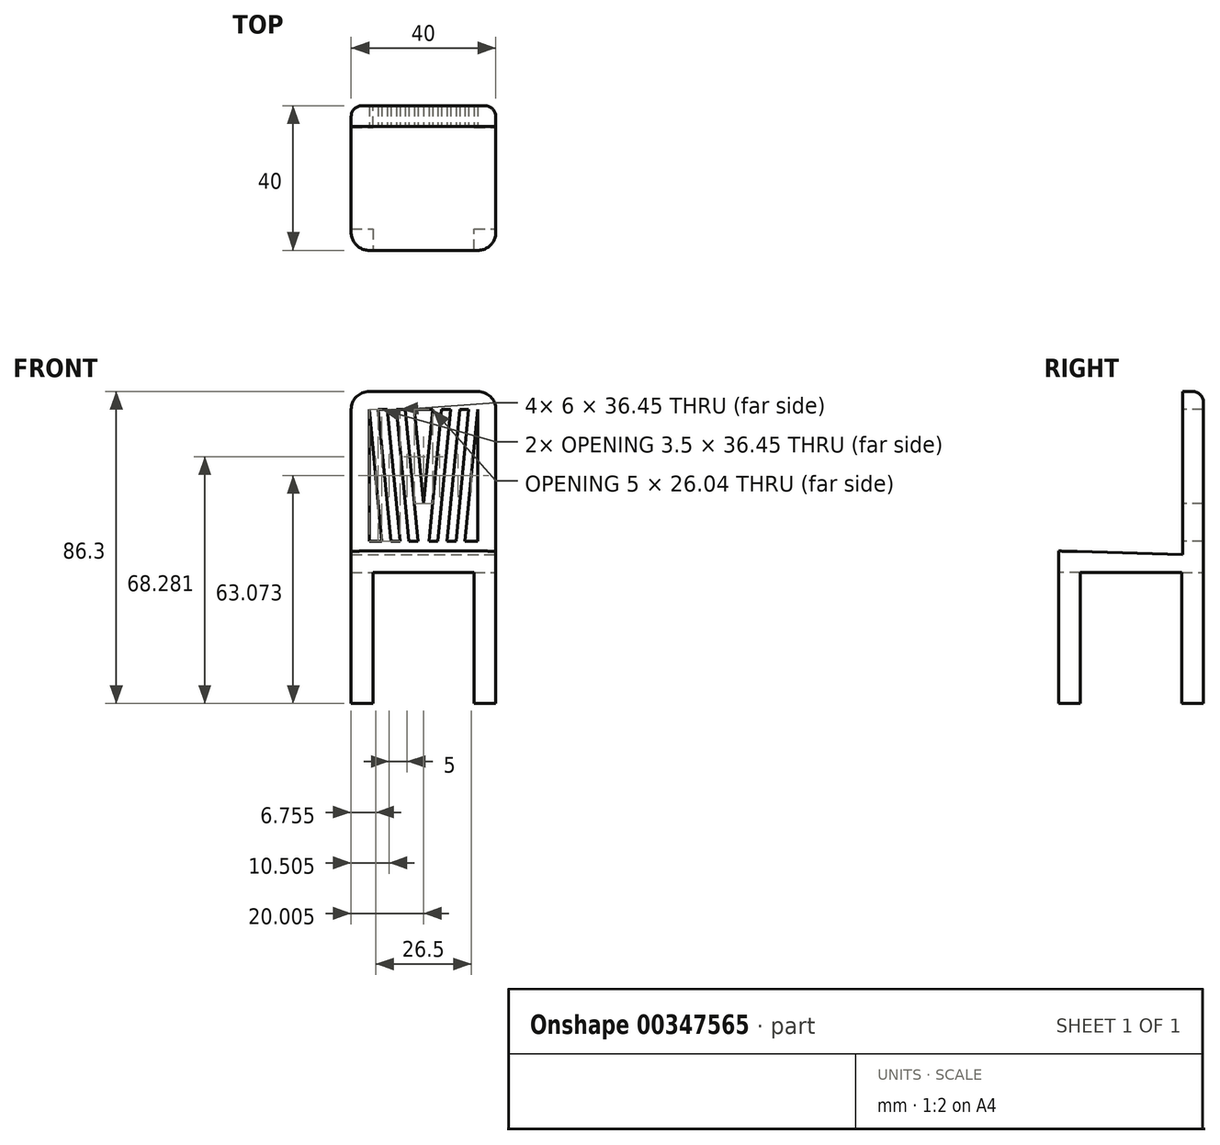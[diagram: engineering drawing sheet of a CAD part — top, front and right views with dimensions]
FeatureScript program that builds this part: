
annotation { "Feature Type Name" : "Feature", "Feature Type Description" : "" }
export const myFeature = defineFeature(function(context is Context, id is Id, definition is map)
    precondition{}
    {
        {
            var Q0;
            Q0=qCreatedBy(makeId("Top.planeOp"),FACE);
            var sketch = newSketch(context, id + "F0", { "sketchPlane" : qUnion([Q0])});
            skLineSegment(sketch, "E0", {"start": v(-30.46, 0) * mm, "end": v(-30.46, 30) * mm});
            skLineSegment(sketch, "E1", {"start": v(-30.46, 30) * mm, "end": v(9.54, 30) * mm});
            skLineSegment(sketch, "E2", {"start": v(9.54, 30) * mm, "end": v(9.54, -10) * mm});
            skLineSegment(sketch, "E3", {"start": v(9.54, -10) * mm, "end": v(-30.46, -10) * mm});
            skLineSegment(sketch, "E4", {"start": v(-30.46, -10) * mm, "end": v(-30.46, 0) * mm});
            skSolve(sketch);
        }
        {
            var Q0;
            Q0=makeQuery(id+"F0.imprint","IMPRINT",FACE,{"disambiguationData":[TD([[makeQuery(id+"F0.imprint","IMPRINT",EDGE,{"derivedFrom":sQuery(id+"F0.wireOp",EDGE,"E0")}),-1.0]])]});
            extrude(context, id + "F1", {"entities" : qUnion([Q0]), "depth" : 6 * mm});
        }
        {
            var Q0;
            Q0=makeQuery(id+"F1.opExtrude","SWEPT_EDGE",EDGE,{"disambiguationData":[OSD([sQuery(id+"F0.wireOp",EDGE,"E3"),sQuery(id+"F0.wireOp",EDGE,"E4")])]});
            var Q1;
            Q1=makeQuery(id+"F1.opExtrude","SWEPT_EDGE",EDGE,{"disambiguationData":[OSD([sQuery(id+"F0.wireOp",EDGE,"E2"),sQuery(id+"F0.wireOp",EDGE,"E3")])]});
            fillet(context, id + "F2", {"entities" : qUnion([Q0, Q1]), "radius" : 5 * mm, "tangentPropagation" : true, "allowEdgeOverflow" : false});
        }
        {
            var Q0;
            Q0=makeQuery(id+"F1.opExtrude","CAP_FACE",FACE,{"disambiguationData":[OSD([sQuery(id+"F0.wireOp",EDGE,"E0"),sQuery(id+"F0.wireOp",EDGE,"E1"),sQuery(id+"F0.wireOp",EDGE,"E2"),sQuery(id+"F0.wireOp",EDGE,"E3"),sQuery(id+"F0.wireOp",EDGE,"E4")])],"isStart":false});
            var sketch = newSketch(context, id + "F3", { "sketchPlane" : qUnion([Q0])});
            skLineSegment(sketch, "E5", {"start": v(-30.46, 30) * mm, "end": v(-30.46, 24.3) * mm});
            skLineSegment(sketch, "E6", {"start": v(-30.46, 24.3) * mm, "end": v(9.54, 24.3) * mm});
            skLineSegment(sketch, "E7", {"start": v(9.54, 24.3) * mm, "end": v(9.54, 30) * mm});
            skLineSegment(sketch, "E8", {"start": v(9.54, 30) * mm, "end": v(-30.46, 30) * mm});
            skSolve(sketch);
        }
        {
            var Q0;
            Q0=makeQuery(id+"F3.imprint","IMPRINT",FACE,{"disambiguationData":[TD([[makeQuery(id+"F3.imprint","IMPRINT",EDGE,{"derivedFrom":sQuery(id+"F3.wireOp",EDGE,"E5")}),-1.0]])]});
            extrude(context, id + "F4", {"entities" : qUnion([Q0]), "operationType" : NewBodyOperationType.ADD, "depth" : 44 * mm});
        }
        {
            var Q0;
            Q0=makeQuery(id+"F4.opExtrude","CAP_EDGE",EDGE,{"disambiguationData":[OSD([sQuery(id+"F3.wireOp",EDGE,"E5")])],"isStart":false});
            var Q1;
            Q1=makeQuery(id+"F4.opExtrude","CAP_EDGE",EDGE,{"disambiguationData":[OSD([sQuery(id+"F3.wireOp",EDGE,"E7")])],"isStart":false});
            fillet(context, id + "F5", {"entities" : qUnion([Q0, Q1]), "radius" : 5 * mm, "tangentPropagation" : true, "allowEdgeOverflow" : false});
        }
        {
            var Q0;
            Q0=makeQuery(id+"F4.opExtrude","SWEPT_FACE",FACE,{"disambiguationData":[OSD([sQuery(id+"F3.wireOp",EDGE,"E6")])]});
            var sketch = newSketch(context, id + "F6", { "sketchPlane" : qUnion([Q0])});
            skLineSegment(sketch, "E9", {"start": v(-25.46, 45) * mm, "end": v(-25.46, 8.55) * mm});
            skPoint(sketch, "E10.start.orphan", {"position": v(6.9, 45) * mm});
            skLineSegment(sketch, "E11", {"start": v(-25.46, 45) * mm, "end": v(4.54, 45) * mm});
            skLineSegment(sketch, "E12", {"start": v(4.54, 45) * mm, "end": v(4.54, 8.55) * mm});
            skLineSegment(sketch, "E13", {"start": v(4.54, 8.55) * mm, "end": v(-25.46, 8.55) * mm});
            skLineSegment(sketch, "E14", {"start": v(-25.46, 8.55) * mm, "end": v(-21.96, 8.55) * mm});
            skLineSegment(sketch, "E15", {"start": v(-21.96, 8.55) * mm, "end": v(-25.46, 45) * mm});
            skLineSegment(sketch, "E16", {"start": v(-21.96, 8.55) * mm, "end": v(-19.46, 8.55) * mm});
            skLineSegment(sketch, "E17", {"start": v(-19.46, 8.55) * mm, "end": v(-22.96, 45) * mm});
            skLineSegment(sketch, "E18", {"start": v(4.54, 8.55) * mm, "end": v(1.04, 8.55) * mm});
            skLineSegment(sketch, "E19", {"start": v(1.04, 8.55) * mm, "end": v(4.54, 45) * mm});
            skLineSegment(sketch, "E20", {"start": v(1.04, 8.55) * mm, "end": v(-1.46, 8.55) * mm});
            skLineSegment(sketch, "E21", {"start": v(-1.46, 8.55) * mm, "end": v(2.04, 45) * mm});
            skLineSegment(sketch, "E22", {"start": v(-1.46, 8.55) * mm, "end": v(-3.96, 8.55) * mm});
            skLineSegment(sketch, "E23", {"start": v(-3.96, 8.55) * mm, "end": v(-0.46, 45) * mm});
            skLineSegment(sketch, "E24", {"start": v(-3.96, 8.55) * mm, "end": v(-6.46, 8.55) * mm});
            skLineSegment(sketch, "E25", {"start": v(-6.46, 8.55) * mm, "end": v(-2.96, 45) * mm});
            skLineSegment(sketch, "E26", {"start": v(-19.46, 8.55) * mm, "end": v(-16.96, 8.55) * mm});
            skLineSegment(sketch, "E27", {"start": v(-16.96, 8.55) * mm, "end": v(-20.46, 45) * mm});
            skLineSegment(sketch, "E28", {"start": v(-16.96, 8.55) * mm, "end": v(-14.46, 8.55) * mm});
            skLineSegment(sketch, "E29", {"start": v(-14.46, 8.55) * mm, "end": v(-17.96, 45) * mm});
            skLineSegment(sketch, "E30", {"start": v(-17.96, 45) * mm, "end": v(-15.46, 45) * mm});
            skLineSegment(sketch, "E31", {"start": v(-15.46, 45) * mm, "end": v(-11.96, 8.55) * mm});
            skLineSegment(sketch, "E32", {"start": v(-6.46, 8.55) * mm, "end": v(-8.96, 8.55) * mm});
            skLineSegment(sketch, "E33", {"start": v(-8.96, 8.55) * mm, "end": v(-5.46, 45) * mm});
            skLineSegment(sketch, "E34", {"start": v(-15.46, 45) * mm, "end": v(-12.96, 45) * mm});
            skLineSegment(sketch, "E35", {"start": v(-5.46, 45) * mm, "end": v(-7.96, 45) * mm});
            skLineSegment(sketch, "E36", {"start": v(-7.96, 45) * mm, "end": v(-10.46, 18.96) * mm});
            skLineSegment(sketch, "E37", {"start": v(-12.96, 45) * mm, "end": v(-10.46, 18.96) * mm});
            skSolve(sketch);
        }
        {
            var Q0;
            Q0=makeQuery(id+"F6.imprint","IMPRINT",FACE,{"disambiguationData":[TD([[makeQuery(id+"F6.imprint","IMPRINT",EDGE,{"derivedFrom":sQuery(id+"F6.wireOp",EDGE,"E9")}),1.0]])]});
            var Q1;
            {var subQ0=sQuery(id+"F6.wireOp",EDGE,"E17");Q1=makeQuery(id+"F6.imprint","IMPRINT",FACE,{"disambiguationData":[TD([[makeQuery(id+"F6.imprint","IMPRINT",EDGE,{"derivedFrom":subQ0}),-1.0]])]});}
            var Q2;
            {var subQ0=sQuery(id+"F6.wireOp",EDGE,"E29");Q2=makeQuery(id+"F6.imprint","IMPRINT",FACE,{"disambiguationData":[TD([[makeQuery(id+"F6.imprint","IMPRINT",EDGE,{"derivedFrom":subQ0}),-1.0]])]});}
            var Q3;
            {var subQ0=sQuery(id+"F6.wireOp",EDGE,"E25");Q3=makeQuery(id+"F6.imprint","IMPRINT",FACE,{"disambiguationData":[TD([[makeQuery(id+"F6.imprint","IMPRINT",EDGE,{"derivedFrom":subQ0}),1.0]])]});}
            var Q4;
            {var subQ0=sQuery(id+"F6.wireOp",EDGE,"E21");Q4=makeQuery(id+"F6.imprint","IMPRINT",FACE,{"disambiguationData":[TD([[makeQuery(id+"F6.imprint","IMPRINT",EDGE,{"derivedFrom":subQ0}),1.0]])]});}
            var Q5;
            Q5=makeQuery(id+"F6.imprint","IMPRINT",FACE,{"disambiguationData":[TD([[makeQuery(id+"F6.imprint","IMPRINT",EDGE,{"derivedFrom":sQuery(id+"F6.wireOp",EDGE,"E12")}),-1.0]])]});
            extrude(context, id + "F7", {"entities" : qUnion([Q0, Q1, Q2, Q3, Q4, Q5]), "operationType" : NewBodyOperationType.REMOVE, "oppositeDirection" : true, "depth" : 25 * mm});
        }
        {
            var Q0;
            Q0=makeQuery(id+"F1.opExtrude","CAP_FACE",FACE,{"disambiguationData":[OSD([sQuery(id+"F0.wireOp",EDGE,"E0"),sQuery(id+"F0.wireOp",EDGE,"E1"),sQuery(id+"F0.wireOp",EDGE,"E2"),sQuery(id+"F0.wireOp",EDGE,"E3"),sQuery(id+"F0.wireOp",EDGE,"E4")])],"isStart":true});
            var sketch = newSketch(context, id + "F8", { "sketchPlane" : qUnion([Q0])});
            skLineSegment(sketch, "E38", {"start": v(-30.46, -30) * mm, "end": v(-30.46, -24) * mm});
            skLineSegment(sketch, "E39", {"start": v(-30.46, -24) * mm, "end": v(-24.46, -24) * mm});
            skLineSegment(sketch, "E40", {"start": v(-24.46, -24) * mm, "end": v(-24.46, -30) * mm});
            skLineSegment(sketch, "E41", {"start": v(-24.46, -30) * mm, "end": v(-30.46, -30) * mm});
            skLineSegment(sketch, "E42", {"start": v(9.54, -30) * mm, "end": v(3.54, -30) * mm});
            skLineSegment(sketch, "E43", {"start": v(3.54, -30) * mm, "end": v(3.54, -24) * mm});
            skLineSegment(sketch, "E44", {"start": v(3.54, -24) * mm, "end": v(9.54, -24) * mm});
            skLineSegment(sketch, "E45", {"start": v(9.54, -24) * mm, "end": v(9.54, -30) * mm});
            skLineSegment(sketch, "E46", {"start": v(3.54, 10) * mm, "end": v(3.54, 4) * mm});
            skLineSegment(sketch, "E47", {"start": v(3.54, 4) * mm, "end": v(9.54, 4) * mm});
            skLineSegment(sketch, "E48", {"start": v(9.54, 4) * mm, "end": v(9.54, 10) * mm});
            skLineSegment(sketch, "E49", {"start": v(9.54, 10) * mm, "end": v(3.54, 10) * mm});
            skLineSegment(sketch, "E50", {"start": v(-30.46, 4) * mm, "end": v(-24.46, 4) * mm});
            skLineSegment(sketch, "E51", {"start": v(-24.46, 4) * mm, "end": v(-24.46, 10) * mm});
            skLineSegment(sketch, "E52", {"start": v(-24.46, 10) * mm, "end": v(-30.46, 10) * mm});
            skLineSegment(sketch, "E53", {"start": v(-30.46, 10) * mm, "end": v(-30.46, 4) * mm});
            skSolve(sketch);
        }
        {
            var Q0;
            {var subQ7=sQuery(id+"F8.wireOp",EDGE,"E50");Q0=makeQuery(id+"F8.imprint","IMPRINT",FACE,{"disambiguationData":[TD([[makeQuery(id+"F8.imprint","IMPRINT",EDGE,{"derivedFrom":subQ7}),1.0]])]});}
            var Q1;
            {var subQ4=sQuery(id+"F8.wireOp",EDGE,"E46");Q1=makeQuery(id+"F8.imprint","IMPRINT",FACE,{"disambiguationData":[TD([[makeQuery(id+"F8.imprint","IMPRINT",EDGE,{"derivedFrom":subQ4}),1.0]])]});}
            var Q2;
            Q2=makeQuery(id+"F8.imprint","IMPRINT",FACE,{"disambiguationData":[TD([[makeQuery(id+"F8.imprint","IMPRINT",EDGE,{"derivedFrom":sQuery(id+"F8.wireOp",EDGE,"E38")}),1.0]])]});
            var Q3;
            Q3=makeQuery(id+"F8.imprint","IMPRINT",FACE,{"disambiguationData":[TD([[makeQuery(id+"F8.imprint","IMPRINT",EDGE,{"derivedFrom":sQuery(id+"F8.wireOp",EDGE,"E42")}),1.0]])]});
            extrude(context, id + "F9", {"entities" : qUnion([Q0, Q1, Q2, Q3]), "operationType" : NewBodyOperationType.ADD, "depth" : 36.3 * mm});
        }
        {
            var Q0;
            Q0=makeQuery(id+"F9.boolean.opBoolean","MERGE",EDGE,{"derivedFrom":[makeQuery(id+"F4.boolean.opBoolean","MERGE",EDGE,{"derivedFrom":[makeQuery(id+"F1.opExtrude","SWEPT_EDGE",EDGE,{"disambiguationData":[OSD([sQuery(id+"F0.wireOp",EDGE,"E1"),sQuery(id+"F0.wireOp",EDGE,"E2")])]}),makeQuery(id+"F4.opExtrude","SWEPT_EDGE",EDGE,{"disambiguationData":[OSD([sQuery(id+"F3.wireOp",EDGE,"E7"),sQuery(id+"F3.wireOp",EDGE,"E8")])]})]}),makeQuery(id+"F9.opExtrude","SWEPT_EDGE",EDGE,{"disambiguationData":[OSD([sQuery(id+"F8.wireOp",EDGE,"E42"),sQuery(id+"F8.wireOp",EDGE,"E45")])]})]});
            fillet(context, id + "F10", {"entities" : qUnion([Q0]), "radius" : 3 * mm, "tangentPropagation" : true, "allowEdgeOverflow" : false});
        }
        {
            var Q0;
            {var subQ2=sQuery(id+"F6.wireOp",EDGE,"E36");Q0=makeQuery(id+"F6.imprint","IMPRINT",FACE,{"disambiguationData":[TD([[makeQuery(id+"F6.imprint","IMPRINT",EDGE,{"derivedFrom":subQ2}),-1.0]])]});}
            extrude(context, id + "F11", {"entities" : qUnion([Q0]), "operationType" : NewBodyOperationType.REMOVE, "oppositeDirection" : true, "depth" : 25 * mm});
        }
        {
            var Q0;
            Q0=makeQuery(id+"F9.boolean.opBoolean","MERGE",FACE,{"derivedFrom":[makeQuery(id+"F4.boolean.opBoolean","MERGE",FACE,{"derivedFrom":[makeQuery(id+"F1.opExtrude","SWEPT_FACE",FACE,{"disambiguationData":[OSD([sQuery(id+"F0.wireOp",EDGE,"E2")])]}),makeQuery(id+"F4.opExtrude","SWEPT_FACE",FACE,{"disambiguationData":[OSD([sQuery(id+"F3.wireOp",EDGE,"E7")])]})]}),makeQuery(id+"F9.opExtrude","SWEPT_FACE",FACE,{"disambiguationData":[OSD([sQuery(id+"F8.wireOp",EDGE,"E45")])]}),makeQuery(id+"F9.opExtrude","SWEPT_FACE",FACE,{"disambiguationData":[OSD([sQuery(id+"F8.wireOp",EDGE,"E48")])]})]});
            var sketch = newSketch(context, id + "F12", { "sketchPlane" : qUnion([Q0])});
            skLineSegment(sketch, "E54", {"start": v(-13.07, 5.97) * mm, "end": v(24.3, 4.87) * mm});
            skLineSegment(sketch, "E55", {"start": v(24.3, 4.87) * mm, "end": v(24.3, 7.6) * mm});
            skLineSegment(sketch, "E56", {"start": v(24.3, 7.6) * mm, "end": v(-13.07, 5.97) * mm});
            skSolve(sketch);
        }
        {
            var Q0;
            {var subQ4=sQuery(id+"F0.wireOp",EDGE,"E2");var subQ7=makeQuery(id+"F1.opExtrude","CAP_EDGE",EDGE,{"disambiguationData":[OSD([subQ4])],"isStart":false});Q0=makeQuery(id+"F12.imprint","IMPRINT",FACE,{"disambiguationData":[TD([[makeQuery(id+"F12.imprint","IMPRINT",EDGE,{"derivedFrom":subQ7}),1.0]])]});}
            var Q1;
            {var subQ0=sQuery(id+"F12.wireOp",EDGE,"E56");Q1=makeQuery(id+"F12.imprint","IMPRINT",FACE,{"disambiguationData":[TD([[makeQuery(id+"F12.imprint","IMPRINT",EDGE,{"derivedFrom":subQ0}),1.0]])]});}
            extrude(context, id + "F13", {"entities" : qUnion([Q0, Q1]), "operationType" : NewBodyOperationType.REMOVE, "oppositeDirection" : true, "depth" : 49.1 * mm});
        }
    });
